annotation { "Feature Type Name" : "Feature", "Feature Type Description" : "" }
export const myFeature = defineFeature(function(context is Context, id is Id, definition is map)
    precondition{}
    {
        {
            var Q0;
            Q0=qCreatedBy(makeId("Top.planeOp"),FACE);
            var sketch = newSketch(context, id + "F0", { "sketchPlane" : qUnion([Q0])});
            skLineSegment(sketch, "E0.bottom", {"start": v(-574.62, 371.73) * mm, "end": v(568.38, 371.73) * mm});
            skLineSegment(sketch, "E0.top", {"start": v(-574.62, -382.12) * mm, "end": v(568.38, -382.12) * mm});
            skLineSegment(sketch, "E0.left", {"start": v(-574.62, 371.73) * mm, "end": v(-574.62, -382.12) * mm});
            skLineSegment(sketch, "E0.right", {"start": v(568.38, 371.73) * mm, "end": v(568.38, -382.12) * mm});
            skText(sketch, "E1", { "text": "Alain Chain Music", "fontName": "Arimo-Regular.ttf"});
            const initialGuessF0  = {"E1": [-2.9093, -0.2113, 1, 0, 0.4494]};
            skSetInitialGuess(sketch, initialGuessF0);
            skSolve(sketch);
        }
        {
            var Q0;
            {var subQ5=sQuery(id+"F0.wireOp",EDGE,"E0.bottom");Q0=makeQuery(id+"F0.imprint","IMPRINT",FACE,{"disambiguationData":[TD([[makeQuery(id+"F0.imprint","IMPRINT",EDGE,{"derivedFrom":subQ5}),-1.0]])]});}
            extrude(context, id + "F1", {"entities" : qUnion([Q0]), "depth" : 12.7 * mm, "offsetDistance" : 25.4 * mm});
        }
        {
            var Q0;
            Q0=makeQuery(id+"F1.opExtrude","CAP_FACE",FACE,{"disambiguationData":[OSD([sQuery(id+"F0.wireOp",EDGE,"E0.bottom"),sQuery(id+"F0.wireOp",EDGE,"E0.top"),sQuery(id+"F0.wireOp",EDGE,"E0.left"),sQuery(id+"F0.wireOp",EDGE,"E0.right"),sQuery(id+"F0.wireOp",EDGE,"E1.sketch_text.stroke-121"),sQuery(id+"F0.wireOp",EDGE,"E1.sketch_text.stroke-122"),sQuery(id+"F0.wireOp",EDGE,"E1.sketch_text.stroke-123"),sQuery(id+"F0.wireOp",EDGE,"E1.sketch_text.stroke-124"),sQuery(id+"F0.wireOp",EDGE,"E1.sketch_text.stroke-125"),sQuery(id+"F0.wireOp",EDGE,"E1.sketch_text.stroke-126"),sQuery(id+"F0.wireOp",EDGE,"E1.sketch_text.stroke-127"),sQuery(id+"F0.wireOp",EDGE,"E1.sketch_text.stroke-128"),sQuery(id+"F0.wireOp",EDGE,"E1.sketch_text.stroke-129"),sQuery(id+"F0.wireOp",EDGE,"E1.sketch_text.stroke-130"),sQuery(id+"F0.wireOp",EDGE,"E1.sketch_text.stroke-131"),sQuery(id+"F0.wireOp",EDGE,"E1.sketch_text.stroke-132"),sQuery(id+"F0.wireOp",EDGE,"E1.sketch_text.stroke-133"),sQuery(id+"F0.wireOp",EDGE,"E1.sketch_text.stroke-134"),sQuery(id+"F0.wireOp",EDGE,"E1.sketch_text.stroke-135"),sQuery(id+"F0.wireOp",EDGE,"E1.sketch_text.stroke-136"),sQuery(id+"F0.wireOp",EDGE,"E1.sketch_text.stroke-137"),sQuery(id+"F0.wireOp",EDGE,"E1.sketch_text.stroke-138"),sQuery(id+"F0.wireOp",EDGE,"E1.sketch_text.stroke-139"),sQuery(id+"F0.wireOp",EDGE,"E1.sketch_text.stroke-140"),sQuery(id+"F0.wireOp",EDGE,"E1.sketch_text.stroke-141"),sQuery(id+"F0.wireOp",EDGE,"E1.sketch_text.stroke-142"),sQuery(id+"F0.wireOp",EDGE,"E1.sketch_text.stroke-143"),sQuery(id+"F0.wireOp",EDGE,"E1.sketch_text.stroke-144"),sQuery(id+"F0.wireOp",EDGE,"E1.sketch_text.stroke-145"),sQuery(id+"F0.wireOp",EDGE,"E1.sketch_text.stroke-156"),sQuery(id+"F0.wireOp",EDGE,"E1.sketch_text.stroke-157"),sQuery(id+"F0.wireOp",EDGE,"E1.sketch_text.stroke-158"),sQuery(id+"F0.wireOp",EDGE,"E1.sketch_text.stroke-159"),sQuery(id+"F0.wireOp",EDGE,"E1.sketch_text.stroke-160"),sQuery(id+"F0.wireOp",EDGE,"E1.sketch_text.stroke-161"),sQuery(id+"F0.wireOp",EDGE,"E1.sketch_text.stroke-162"),sQuery(id+"F0.wireOp",EDGE,"E1.sketch_text.stroke-163"),sQuery(id+"F0.wireOp",EDGE,"E1.sketch_text.stroke-164"),sQuery(id+"F0.wireOp",EDGE,"E1.sketch_text.stroke-165"),sQuery(id+"F0.wireOp",EDGE,"E1.sketch_text.stroke-166"),sQuery(id+"F0.wireOp",EDGE,"E1.sketch_text.stroke-167"),sQuery(id+"F0.wireOp",EDGE,"E1.sketch_text.stroke-168"),sQuery(id+"F0.wireOp",EDGE,"E1.sketch_text.stroke-169"),sQuery(id+"F0.wireOp",EDGE,"E1.sketch_text.stroke-170"),sQuery(id+"F0.wireOp",EDGE,"E1.sketch_text.stroke-171"),sQuery(id+"F0.wireOp",EDGE,"E1.sketch_text.stroke-172"),sQuery(id+"F0.wireOp",EDGE,"E1.sketch_text.stroke-173"),sQuery(id+"F0.wireOp",EDGE,"E1.sketch_text.stroke-174"),sQuery(id+"F0.wireOp",EDGE,"E1.sketch_text.stroke-175"),sQuery(id+"F0.wireOp",EDGE,"E1.sketch_text.stroke-176"),sQuery(id+"F0.wireOp",EDGE,"E1.sketch_text.stroke-177"),sQuery(id+"F0.wireOp",EDGE,"E1.sketch_text.stroke-178"),sQuery(id+"F0.wireOp",EDGE,"E1.sketch_text.stroke-179"),sQuery(id+"F0.wireOp",EDGE,"E1.sketch_text.stroke-180"),sQuery(id+"F0.wireOp",EDGE,"E1.sketch_text.stroke-181"),sQuery(id+"F0.wireOp",EDGE,"E1.sketch_text.stroke-182"),sQuery(id+"F0.wireOp",EDGE,"E1.sketch_text.stroke-183"),sQuery(id+"F0.wireOp",EDGE,"E1.sketch_text.stroke-184"),sQuery(id+"F0.wireOp",EDGE,"E1.sketch_text.stroke-191"),sQuery(id+"F0.wireOp",EDGE,"E1.sketch_text.stroke-192"),sQuery(id+"F0.wireOp",EDGE,"E1.sketch_text.stroke-193"),sQuery(id+"F0.wireOp",EDGE,"E1.sketch_text.stroke-194"),sQuery(id+"F0.wireOp",EDGE,"E1.sketch_text.stroke-195"),sQuery(id+"F0.wireOp",EDGE,"E1.sketch_text.stroke-196"),sQuery(id+"F0.wireOp",EDGE,"E1.sketch_text.stroke-197"),sQuery(id+"F0.wireOp",EDGE,"E1.sketch_text.stroke-198")])],"isStart":false});
            var sketch = newSketch(context, id + "F2", { "sketchPlane" : qUnion([Q0])});
            skText(sketch, "E2", { "text": "Alain", "fontName": "NotoSans-Regular.ttf"});
            const initialGuessF2  = {"E2": [0.2976, -0.17229, 1, 0, 0.24966]};
            skSetInitialGuess(sketch, initialGuessF2);
            skSolve(sketch);
        }
        {
            var Q0;
            Q0 = qSketchRegion(id + "F2", true);
            extrude(context, id + "F3", {"entities" : qUnion([Q0]), "operationType" : NewBodyOperationType.ADD, "depth" : 25.4 * mm, "offsetDistance" : 25.4 * mm});
        }
    });